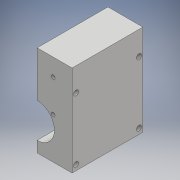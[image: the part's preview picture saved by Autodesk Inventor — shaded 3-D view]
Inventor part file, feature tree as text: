
AUTODESK INVENTOR PART (.ipt)
format: ipt  version: 2018 (Build 220112000, 112)  size: 416,256 bytes
history: native  units: mm
features: sketch x21, projected_geometry x20, extrude x17, hole x4, fillet x3, chamfer x1
ambient origin geometry x8: Origin, YZ Plane, XZ Plane, XY Plane, X Axis, Y Axis, Z Axis, Center Point
bodies: Solid1 (feature_tree)
feature tree (66):
  extrude  "Extrusion1"  Depth=45.0mm
  extrude  "Extrusion2"  Depth=1.95mm
  hole  "Hole1"  [1 undecoded]
  hole  "Hole2"  [1 undecoded]
  fillet  "Fillet1"  Radius=14.0mm
  extrude  "Extrusion3"  Depth=18.5mm
  extrude  "Extrusion4"  Depth=10.0mm
  extrude  "Extrusion5"  Depth=2.195mm
  extrude  "Extrusion6"  Depth=20.5mm
  hole  "Hole3"  [1 undecoded]
  extrude  "Extrusion7"  Depth=0.5mm
  extrude  "Extrusion8"  Depth=5.0mm TaperAngle=0.0deg
  extrude  "Extrusion9"  Depth=10.0mm
  extrude  "Extrusion10"  Depth=10.0mm
  extrude  "Extrusion11"  Depth=14.5mm
  extrude  "Extrusion12"  Depth=14.5mm
  extrude  "Extrusion13"  Depth=5.0mm
  extrude  "Extrusion14"  Depth=5.0mm
  extrude  "Extrusion15"  Depth=5.0mm
  extrude  "Extrusion16"  Depth=9.0mm
  extrude  "Extrusion17"  Depth=14.75mm
  chamfer  "Chamfer1"  Distance=4.0mm
  fillet  "Fillet7"  Radius=1.0mm
  hole  "Hole4"  [1 undecoded]
  fillet  "Fillet8"  Radius=32.0mm
  sketch  "Sketch1"  dims[d0=24.5mm d1=45.0mm]
  sketch  "Sketch2"  dims[d2=1.95mm d3=0.0mm d4=2.25mm]
  projected_geometry  "Projected Loop1"
  sketch  "Sketch3"  dims[d5=20.0mm d6=2.25mm]
  projected_geometry  "Projected Loop2"
  sketch  "Sketch4"  dims[d7=5.25mm d8=5.25mm d9=14.0mm]
  projected_geometry  "Projected Loop3"
  sketch  "Sketch5"  dims[d10=5.25mm d11=18.5mm]
  projected_geometry  "Projected Loop4"
  sketch  "Sketch6"  dims[d12=10.0mm d13=0.0mm d14=20.5mm]
  projected_geometry  "Projected Loop5"
  sketch  "Sketch7"  dims[d15=2.0mm d16=2.195mm]
  projected_geometry  "Projected Loop6"
  sketch  "Sketch8"  dims[d17=2.0mm]
  projected_geometry  "Projected Loop7"
  sketch  "Sketch9"  dims[d18=2.4mm d19=6.0mm d20=4.4mm d21=2.0mm d22=90.0deg d23=8.0mm d24=20.594885mm d25=20.5mm]
  projected_geometry  "Projected Loop8"
  projected_geometry  "Projected Loop9"
  sketch  "Sketch10"  dims[d26=26.65mm d27=2.0mm]
  projected_geometry  "Projected Loop10"
  projected_geometry  "Projected Loop11"
  sketch  "Sketch11"  dims[d28=2.0mm]
  projected_geometry  "Projected Loop12"
  sketch  "Sketch12"  dims[d29=2.4mm d30=6.0mm d31=4.4mm d32=2.0mm d33=90.0deg d34=8.0mm d35=20.594885mm d36=0.5mm]
  sketch  "Sketch13"  dims[d37=18.0mm d38=5.0mm d39=0.0mm]
  sketch  "Sketch14"  dims[d41=10.0mm d42=0.0mm d43=24.5mm]
  projected_geometry  "Projected Loop13"
  sketch  "Sketch15"  dims[d44=1.15mm d45=0.0mm d46=10.0mm]
  sketch  "Sketch16"  dims[d47=22.0mm d48=14.5mm]
  projected_geometry  "Projected Loop14"
  sketch  "Sketch17"  dims[d49=20.0mm d50=14.5mm]
  projected_geometry  "Projected Loop15"
  sketch  "Sketch18"  dims[d51=24.5mm d52=5.0mm]
  projected_geometry  "Projected Loop16"
  sketch  "Sketch19"  dims[d53=5.0mm d54=2.25mm]
  projected_geometry  "Projected Loop17"
  sketch  "Sketch20"  dims[d55=2.25mm d56=5.0mm]
  projected_geometry  "Projected Loop18"
  sketch  "Sketch21"  dims[d57=5.0mm d58=9.0mm d59=14.75mm d60=4.0mm d61=1.0mm d62=0.0mm d63=20.7mm d64=2.4mm d65=6.0mm d66=4.4mm d67=2.0mm d68=90.0deg d69=8.0mm d70=20.594885mm d72=32.0mm d73=5.0mm d74=0.0mm d75=1.0mm d76=0.0mm d77=12.25mm d78=0.0mm d80=8.0mm d81=4.5mm d82=0.0mm d84=0.2mm d85=0.0mm d86=22.0mm d87=0.5mm d88=0.0mm d91=8.0mm d92=0.0mm d93=5.0mm d94=0.0mm d95=5.0mm d96=0.0mm d98=0.2mm d99=0.0mm d100=0.2mm d101=0.0mm d102=2.5mm d103=2.0mm d104=45.0deg d105=1.5mm d106=8.0mm d107=3.2mm d108=5.029mm d109=6.3mm d110=2.0mm d111=90.0deg d112=7.675mm d113=20.594885mm d114=0.5mm]
  projected_geometry  "Projected Loop19"
  projected_geometry  "Projected Loop20"
note: 4 required parameter values undecoded (feature->parameter linkage not recoverable at this tier; creation-order binding heuristic only, values carry confidence <= 0.55)
